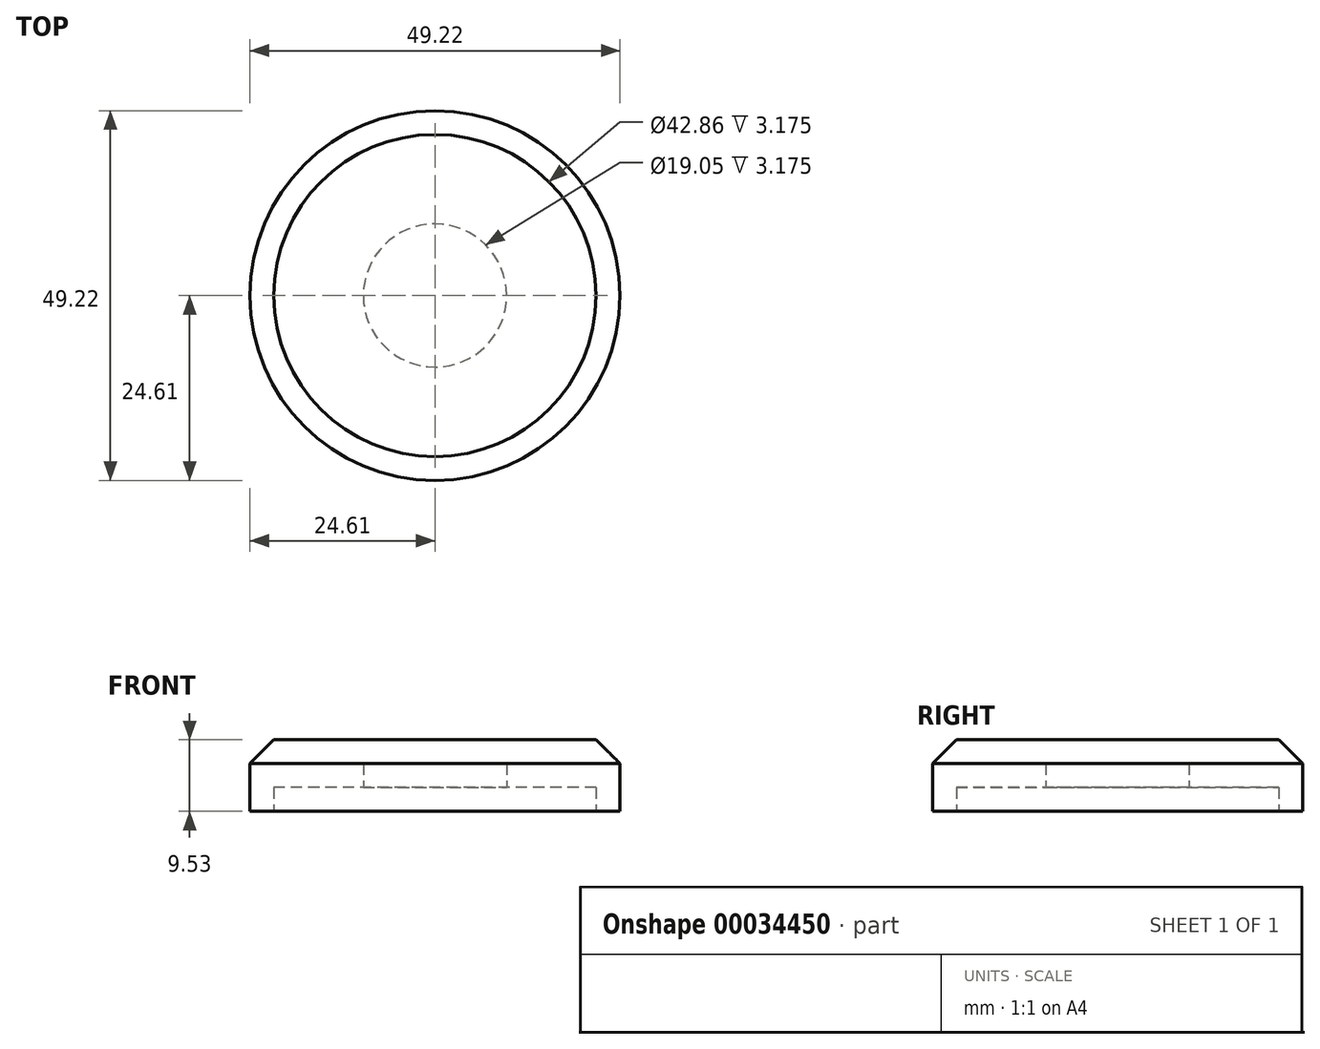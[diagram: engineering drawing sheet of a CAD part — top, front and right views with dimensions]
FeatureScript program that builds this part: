
annotation { "Feature Type Name" : "Feature", "Feature Type Description" : "" }
export const myFeature = defineFeature(function(context is Context, id is Id, definition is map)
    precondition{}
    {
        {
            var Q0;
            Q0=qCreatedBy(makeId("Top.planeOp"),FACE);
            var sketch = newSketch(context, id + "F0", { "sketchPlane" : qUnion([Q0])});
            skCircle(sketch, "E0", {"center": v(0, 0) * mm, "radius": 21.43 * mm, "construction": true});
            skCircle(sketch, "E1", {"center": v(0, 0) * mm, "radius": 24.6 * mm});
            skSolve(sketch);
        }
        {
            var Q0;
            Q0=makeQuery(id+"F0.imprint","IMPRINT",FACE,{"disambiguationData":[TD([[makeQuery(id+"F0.imprint","IMPRINT",EDGE,{"derivedFrom":sQuery(id+"F0.wireOp",EDGE,"E1")}),1.0]])]});
            extrude(context, id + "F1", {"entities" : qUnion([Q0]), "depth" : 9.52 * mm});
        }
        {
            var Q0;
            Q0=makeQuery(id+"F0.imprint","IMPRINT",FACE,{"disambiguationData":[TD([[makeQuery(id+"F0.imprint","IMPRINT",EDGE,{"derivedFrom":sQuery(id+"F0.wireOp",EDGE,"E1")}),1.0]])]});
            var sketch = newSketch(context, id + "F2", { "sketchPlane" : qUnion([Q0])});
            skCircle(sketch, "E2.0", {"center": v(0, 0) * mm, "radius": 21.43 * mm});
            skSolve(sketch);
        }
        {
            var Q0;
            Q0=makeQuery(id+"F2.imprint","IMPRINT",FACE,{"disambiguationData":[TD([[makeQuery(id+"F2.imprint","IMPRINT",EDGE,{"derivedFrom":sQuery(id+"F2.wireOp",EDGE,"E2.0")}),1.0]])]});
            var Q1;
            Q1=sQuery(id+"F2.wireOp",EDGE,"E2.0");
            extrude(context, id + "F3", {"entities" : qUnion([Q0]), "operationType" : NewBodyOperationType.REMOVE, "surfaceEntities" : qUnion([Q1]), "depth" : 3.17 * mm});
        }
        {
            var Q0;
            Q0=makeQuery(id+"F3.boolean.opBoolean","COPY",FACE,{"derivedFrom":makeQuery(id+"F3.opExtrude","CAP_FACE",FACE,{"disambiguationData":[OSD([sQuery(id+"F2.wireOp",EDGE,"E2.0")])],"isStart":false})});
            var sketch = newSketch(context, id + "F4", { "sketchPlane" : qUnion([Q0])});
            skCircle(sketch, "E3", {"center": v(0, 0) * mm, "radius": 9.52 * mm});
            skSolve(sketch);
        }
        {
            var Q0;
            Q0 = qSketchRegion(id + "F4", true);
            extrude(context, id + "F5", {"entities" : qUnion([Q0]), "operationType" : NewBodyOperationType.REMOVE, "oppositeDirection" : true, "depth" : 3.17 * mm});
        }
        {
            var Q0;
            Q0=makeQuery(id+"F1.opExtrude","CAP_EDGE",EDGE,{"disambiguationData":[OSD([sQuery(id+"F0.wireOp",EDGE,"E1")])],"isStart":false});
            chamfer(context, id + "F6", {"entities" : qUnion([Q0]), "width" : 3.17 * mm, "tangentPropagation" : true});
        }
    });
